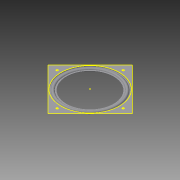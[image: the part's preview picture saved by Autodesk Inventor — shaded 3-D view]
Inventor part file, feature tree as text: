
AUTODESK INVENTOR PART (.ipt)
format: ipt  version: 2015 (Build 190159000, 159)  size: 149,504 bytes
history: native  units: in
note: dims shown in document units (in); Inventor stores cm internally (conversion verified against a paired STEP export)
features: other x1, sketch x1, imported_body x1
ambient origin geometry x8: Origin, YZ Plane, XZ Plane, XY Plane, X Axis, Y Axis, Z Axis, Center Point
bodies: Solid1 (feature_tree)
feature tree (3):
  other  "1544T100.sat1"
  sketch  "Sketch1"
  imported_body  "Base1"
